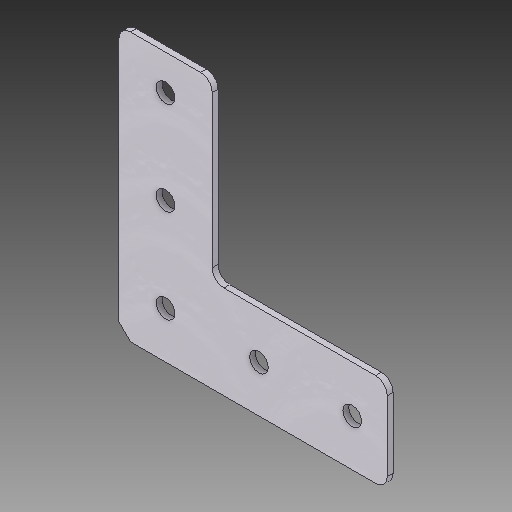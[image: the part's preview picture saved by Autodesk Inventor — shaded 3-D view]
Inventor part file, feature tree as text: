
AUTODESK INVENTOR PART (.ipt)
format: ipt  version: 2019 (Build 230136000, 136)  size: 183,296 bytes
history: native  units: in
note: dims shown in document units (in); Inventor stores cm internally (conversion verified against a paired STEP export)
features: extrude x3, sketch x3, fillet x1, chamfer x1
ambient origin geometry x8: Origin, YZ Plane, XZ Plane, XY Plane, X Axis, Y Axis, Z Axis, Center Point
bodies: Solid1 (feature_tree)
feature tree (8):
  extrude  "Extrusion1"  Depth=1.0in TaperAngle=0.0deg
  extrude  "Extrusion2"  Depth=0.125in
  extrude  "Extrusion3"  Depth=1.0in TaperAngle=0.0deg
  fillet  "Fillet2"  Radius=0.125in
  sketch  "Sketch1"  dims[d0=0.125in d1=1.0in d2=0.0in]
  sketch  "Sketch2"  dims[d4=0.0175in d5=0.0in d6=0.125in]
  sketch  "Sketch3"  dims[d7=0.125in d8=1.0in d9=0.0in d10=0.125in]
  chamfer  "Chamfer2"  [1 undecoded]
note: 1 required parameter value undecoded (feature->parameter linkage not recoverable at this tier; creation-order binding heuristic only, values carry confidence <= 0.55)
